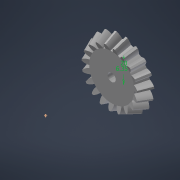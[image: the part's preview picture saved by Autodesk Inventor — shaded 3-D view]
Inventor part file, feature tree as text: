
AUTODESK INVENTOR PART (.ipt)
format: ipt  version: 2022 (Build 260153000, 153)  size: 569,856 bytes
history: native  units: mm
features: other x24, loft x2, pattern_circular x2, sketch x2, extrude x2, chamfer x1
ambient origin geometry x6: Origin, XZ Plane, X Axis, Y Axis, Z Axis, Center Point
bodies: Solid1 (feature_tree)
feature tree (33):
  other  "Top Point"
  other  "Mesh Plane2"
  other  "Teeth Body"
  other  "Start Point"
  other  "Tooth Plane"
  other  "Start Sketch"
  other  "End Point"
  other  "3D Sketch Right"
  other  "End Plane Right"
  loft  "Loft Right"
  pattern_circular  "Circular Pattern Right"  [2 undecoded]
  other  "3D Sketch Left"
  other  "End Plane Left"
  loft  "Loft Left"
  pattern_circular  "Circular Pattern Left"  Angle=90.0deg  [1 undecoded]
  other  "Fix Body"
  sketch  "Sketch8"  dims[d2=52.149033mm d3=10.0mm d4=59.079879mm d5=90.0deg d7=9.577943mm d8=10.649182mm d9=21.38665mm d11=10.275mm d12=8.052853mm d15=8.953519mm d16=17.981267mm d17=0.0mm d18=90.0deg d19=0.0mm d20=90.0deg d21=190.0mm d22=360.0deg d26=428.686656mm d27=9.553763mm d28=47.5mm d29=-3.769093mm d30=8.052853mm d31=8.953519mm d32=17.981267mm d35=0.0mm d37=0.0mm d39=0.0mm d40=90.0deg d41=190.0mm d42=360.0deg d46=90.0deg d47=90.0deg d48=0.0mm d49=0.0mm d50=90.0deg d51=1.65347mm d52=0.0mm d53=0.0mm d54=0.0mm d56=20.48719mm d57=29.692946mm d58=21.882946mm d59=24.964956mm d60=18.398538mm d61=24.964956mm d62=18.398538mm d65=428.686656mm d66=31.5mm d67=47.5mm d68=-3.769093mm d69=9.553763mm d70=8.953519mm d71=17.981267mm d72=8.052853mm d73=18.398538mm d74=24.964956mm d75=0.0mm d77=0.0mm d79=0.0mm d80=90.0deg d81=190.0mm d82=360.0deg d84=10.0mm d85=20.0mm d86=20.0mm d87=10.0mm d88=0.0mm d89=0.0mm d90=90.0deg d91=90.0deg d92=90.0deg d93=90.0deg d94=6.35mm d95=20.0mm d96=5.0mm d97=0.0mm d98=8.0mm d99=0.0mm d100=3.0mm d101=2.0mm d102=45.0deg]
  extrude  "Extrusion1"  Depth=8.0mm
  extrude  "Extrusion2"  Depth=8.0mm
  chamfer  "Chamfer1"  Distance=21.38665mm
  other  "Mesh Plane"
  other  "Top Plane"
  other  "Teeth Body Sketch"
  other  "End Plane"
  other  "End Sketch"
  other  "Helical Curve Left"
  other  "End Sketch Left"
  other  "Body Sketch"
  sketch  "Sketch6"  dims[d0=47.5mm d1=41.92116mm]
  other  "Srf1"
  other  "Helical Curve Right"
  other  "End Sketch Right"
  other  "Pitch Diameter"
note: 3 required parameter values undecoded (feature->parameter linkage not recoverable at this tier; creation-order binding heuristic only, values carry confidence <= 0.55)
